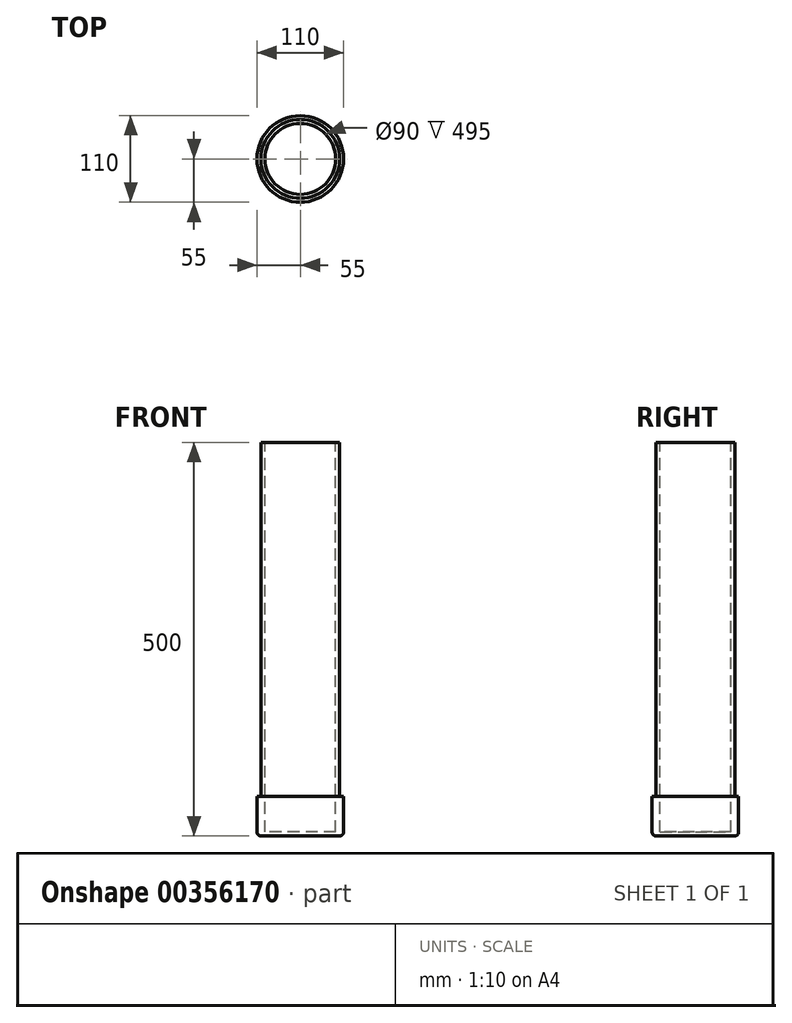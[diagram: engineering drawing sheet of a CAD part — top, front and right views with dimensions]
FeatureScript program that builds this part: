
annotation { "Feature Type Name" : "Feature", "Feature Type Description" : "" }
export const myFeature = defineFeature(function(context is Context, id is Id, definition is map)
    precondition{}
    {
        {
            var Q0;
            Q0=qCreatedBy(makeId("Front.planeOp"),FACE);
            var sketch = newSketch(context, id + "F0", { "sketchPlane" : qUnion([Q0])});
            skLineSegment(sketch, "E0.bottom", {"start": v(0, 0) * mm, "end": v(-50, 0) * mm});
            skLineSegment(sketch, "E0.top", {"start": v(0, 500) * mm, "end": v(-50, 500) * mm});
            skLineSegment(sketch, "E0.left", {"start": v(0, 0) * mm, "end": v(0, 500) * mm});
            skLineSegment(sketch, "E0.right", {"start": v(-50, 0) * mm, "end": v(-50, 500) * mm});
            skLineSegment(sketch, "E1.bottom", {"start": v(-50, 50) * mm, "end": v(-55, 50) * mm});
            skLineSegment(sketch, "E1.top", {"start": v(-50, 0) * mm, "end": v(-50, 0) * mm});
            skLineSegment(sketch, "E1.right", {"start": v(-55, 50) * mm, "end": v(-55, 5) * mm});
            skPoint(sketch, "E2.visualSharp", {"position": v(-55, 0) * mm});
            skArc(sketch, "E2.filletArc", {"start": v(-55, 5) * mm, "mid": v(-53.54, 1.46) * mm, "end": v(-50, 0) * mm});
            skLineSegment(sketch, "E3.bottom", {"start": v(0, 500) * mm, "end": v(-45, 500) * mm});
            skLineSegment(sketch, "E3.top", {"start": v(0, 5) * mm, "end": v(-45, 5) * mm});
            skLineSegment(sketch, "E3.left", {"start": v(0, 500) * mm, "end": v(0, 5) * mm});
            skLineSegment(sketch, "E3.right", {"start": v(-45, 500) * mm, "end": v(-45, 5) * mm});
            skSolve(sketch);
        }
        {
            var Q0;
            {var subQ2=sQuery(id+"F0.wireOp",EDGE,"E1.bottom");Q0=makeQuery(id+"F0.imprint","IMPRINT",FACE,{"disambiguationData":[TD([[makeQuery(id+"F0.imprint","IMPRINT",EDGE,{"derivedFrom":subQ2}),1.0]])]});}
            var Q1;
            {var subQ1=sQuery(id+"F0.wireOp",EDGE,"E0.bottom");Q1=makeQuery(id+"F0.imprint","IMPRINT",FACE,{"disambiguationData":[TD([[makeQuery(id+"F0.imprint","IMPRINT",EDGE,{"derivedFrom":subQ1}),-1.0]])]});}
            var Q2;
            Q2=sQuery(id+"F0.wireOp",EDGE,"E3.left");
            revolve(context, id + "F1", {"entities" : qUnion([Q0, Q1]), "axis" : qUnion([Q2]), "revolveType" : RevolveType.FULL});
        }
    });
